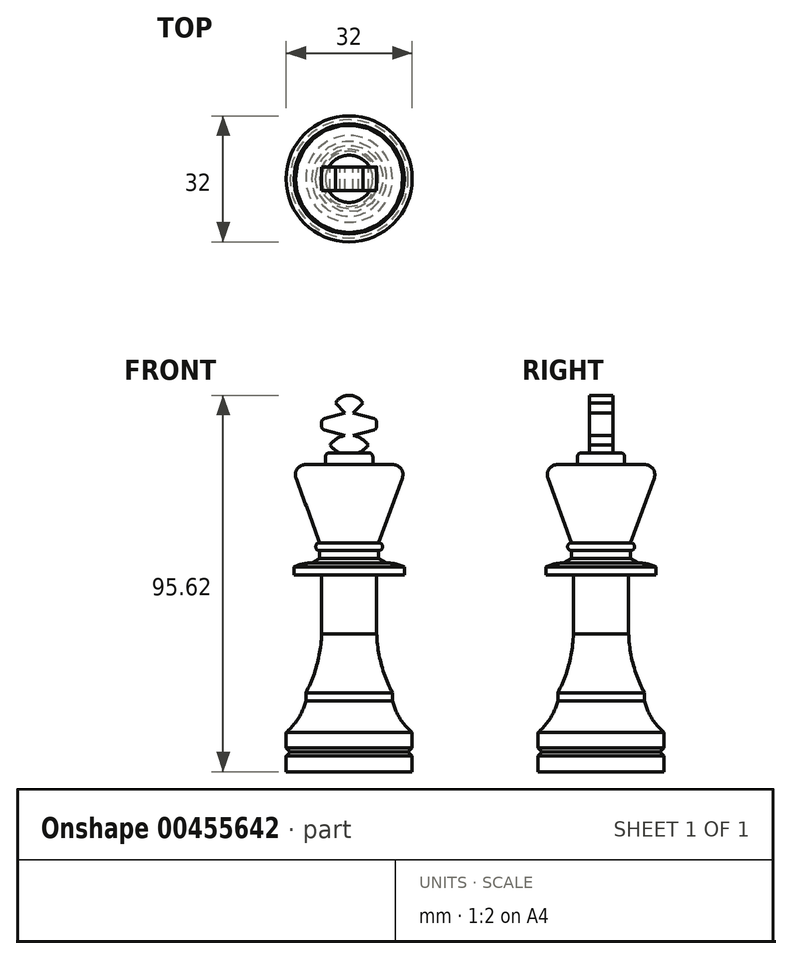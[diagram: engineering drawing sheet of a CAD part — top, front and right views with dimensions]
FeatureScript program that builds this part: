
annotation { "Feature Type Name" : "Feature", "Feature Type Description" : "" }
export const myFeature = defineFeature(function(context is Context, id is Id, definition is map)
    precondition{}
    {
        {
            var Q0;
            Q0=qCreatedBy(makeId("Front.planeOp"),FACE);
            var sketch = newSketch(context, id + "F0", { "sketchPlane" : qUnion([Q0])});
            skLineSegment(sketch, "E0", {"start": v(0, 0) * mm, "end": v(0, 4) * mm});
            skLineSegment(sketch, "E1", {"start": v(0, 4) * mm, "end": v(1, 5) * mm});
            skLineSegment(sketch, "E2", {"start": v(1, 5) * mm, "end": v(0, 6) * mm});
            skLineSegment(sketch, "E3", {"start": v(0, 6) * mm, "end": v(0, 10) * mm});
            skArc(sketch, "E4", {"start": v(0, 10) * mm, "mid": v(3.15, 13.6) * mm, "end": v(5, 18) * mm});
            skLineSegment(sketch, "E5", {"start": v(5, 18) * mm, "end": v(5, 20) * mm});
            skLineSegment(sketch, "E6", {"start": v(5, 20) * mm, "end": v(5, 20) * mm});
            skArc(sketch, "E7", {"start": v(5, 20) * mm, "mid": v(7.84, 27.28) * mm, "end": v(9, 35) * mm});
            skLineSegment(sketch, "E8", {"start": v(16, 0) * mm, "end": v(0, 0) * mm});
            skLineSegment(sketch, "E9", {"start": v(9, 35) * mm, "end": v(9, 50) * mm});
            skLineSegment(sketch, "E10", {"start": v(8.5, 58.16) * mm, "end": v(2.5, 74.64) * mm});
            skLineSegment(sketch, "E11", {"start": v(8.5, 54.16) * mm, "end": v(8.5, 56.16) * mm});
            skArc(sketch, "E12", {"start": v(8.5, 58.16) * mm, "mid": v(7.5, 57.16) * mm, "end": v(8.5, 56.16) * mm});
            skLineSegment(sketch, "E13", {"start": v(4.85, 78) * mm, "end": v(16, 78) * mm});
            skLineSegment(sketch, "E14", {"start": v(16, 0) * mm, "end": v(16, 78) * mm});
            skLineSegment(sketch, "E15", {"start": v(9, 50) * mm, "end": v(2, 50) * mm});
            skLineSegment(sketch, "E16", {"start": v(2, 50) * mm, "end": v(2, 52) * mm});
            skArc(sketch, "E17", {"start": v(4.85, 78) * mm, "mid": v(2.8, 76.93) * mm, "end": v(2.5, 74.64) * mm});
            skArc(sketch, "E18", {"start": v(6.5, 53) * mm, "mid": v(4.2, 52.76) * mm, "end": v(2, 52) * mm});
            skLineSegment(sketch, "E19", {"start": v(6.5, 53) * mm, "end": v(8.5, 54.16) * mm});
            skSolve(sketch);
        }
        {
            var Q0;
            Q0 = qSketchRegion(id + "F0", true);
            var Q1;
            Q1=sQuery(id+"F0.wireOp",EDGE,"E14");
            revolve(context, id + "F1", {"entities" : qUnion([Q0]), "axis" : qUnion([Q1]), "revolveType" : RevolveType.FULL});
        }
        {
            var Q0;
            Q0=makeQuery(id+"F1.opRevolve","SWEPT_FACE",FACE,{"disambiguationData":[OSD([sQuery(id+"F0.wireOp",EDGE,"E13")])]});
            var sketch = newSketch(context, id + "F2", { "sketchPlane" : qUnion([Q0])});
            skCircle(sketch, "E20", {"center": v(16, 0) * mm, "radius": 6 * mm});
            skSolve(sketch);
        }
        {
            var Q0;
            Q0 = qSketchRegion(id + "F2", true);
            extrude(context, id + "F3", {"entities" : qUnion([Q0]), "operationType" : NewBodyOperationType.ADD, "depth" : 3 * mm});
        }
        {
            var Q0;
            Q0=makeQuery(id+"F3.opExtrude","CAP_EDGE",EDGE,{"disambiguationData":[OSD([sQuery(id+"F2.wireOp",EDGE,"E20")])],"isStart":false});
            fillet(context, id + "F4", {"entities" : qUnion([Q0]), "radius" : 1 * mm, "tangentPropagation" : true, "allowEdgeOverflow" : false});
        }
        {
            var Q0;
            Q0=qCreatedBy(makeId("Front.planeOp"),FACE);
            var sketch = newSketch(context, id + "F5", { "sketchPlane" : qUnion([Q0])});
            skArc(sketch, "E21", {"start": v(18.36, 81) * mm, "mid": v(19.75, 81.83) * mm, "end": v(20.86, 83) * mm});
            skArc(sketch, "E22", {"start": v(20.86, 83) * mm, "mid": v(19.17, 84.58) * mm, "end": v(17, 85.4) * mm});
            skLineSegment(sketch, "E23", {"start": v(17, 85.4) * mm, "end": v(23, 87) * mm});
            skLineSegment(sketch, "E24", {"start": v(23, 87) * mm, "end": v(23, 89.5) * mm});
            skLineSegment(sketch, "E25", {"start": v(23, 89.5) * mm, "end": v(17, 91.12) * mm});
            skLineSegment(sketch, "E26", {"start": v(17, 91.12) * mm, "end": v(19.5, 93.62) * mm});
            skArc(sketch, "E27", {"start": v(19.5, 93.62) * mm, "mid": v(18.02, 95.08) * mm, "end": v(16, 95.62) * mm});
            skLineSegment(sketch, "E28", {"start": v(18.36, 81) * mm, "end": v(16, 81) * mm});
            skLineSegment(sketch, "E29", {"start": v(16, 81) * mm, "end": v(16, 95.62) * mm});
            skArc(sketch, "E30.MirrorCS", {"start": v(12.5, 93.62) * mm, "mid": v(13.98, 95.08) * mm, "end": v(16, 95.62) * mm});
            skLineSegment(sketch, "E31.MirrorCS", {"start": v(15, 91.12) * mm, "end": v(12.5, 93.62) * mm});
            skLineSegment(sketch, "E32.MirrorCS", {"start": v(9, 89.5) * mm, "end": v(15, 91.12) * mm});
            skLineSegment(sketch, "E33.MirrorCS", {"start": v(9, 87) * mm, "end": v(9, 89.5) * mm});
            skLineSegment(sketch, "E34.MirrorCS", {"start": v(15, 85.4) * mm, "end": v(9, 87) * mm});
            skArc(sketch, "E35.MirrorCS", {"start": v(11.14, 83) * mm, "mid": v(12.83, 84.58) * mm, "end": v(15, 85.4) * mm});
            skArc(sketch, "E36.MirrorCS", {"start": v(13.64, 81) * mm, "mid": v(12.25, 81.83) * mm, "end": v(11.14, 83) * mm});
            skLineSegment(sketch, "E37.MirrorCS", {"start": v(13.64, 81) * mm, "end": v(16, 81) * mm});
            skSolve(sketch);
        }
        {
            var Q0;
            Q0 = qSketchRegion(id + "F5", true);
            extrude(context, id + "F6", {"entities" : qUnion([Q0]), "depth" : 3 * mm, "hasSecondDirection" : true, "secondDirectionOppositeDirection" : true, "secondDirectionDepth" : 3 * mm});
        }
        {
            var Q0;
            Q0=makeQuery(id+"F6.opExtrude","SWEPT_EDGE",EDGE,{"disambiguationData":[OSD([sQuery(id+"F5.wireOp",EDGE,"E24"),sQuery(id+"F5.wireOp",EDGE,"E25")])]});
            var Q1;
            Q1=makeQuery(id+"F6.opExtrude","SWEPT_EDGE",EDGE,{"disambiguationData":[OSD([sQuery(id+"F5.wireOp",EDGE,"E23"),sQuery(id+"F5.wireOp",EDGE,"E24")])]});
            var Q2;
            Q2=makeQuery(id+"F6.opExtrude","SWEPT_EDGE",EDGE,{"disambiguationData":[OSD([sQuery(id+"F5.wireOp",EDGE,"E32.MirrorCS"),sQuery(id+"F5.wireOp",EDGE,"E33.MirrorCS")])]});
            var Q3;
            Q3=makeQuery(id+"F6.opExtrude","SWEPT_EDGE",EDGE,{"disambiguationData":[OSD([sQuery(id+"F5.wireOp",EDGE,"E33.MirrorCS"),sQuery(id+"F5.wireOp",EDGE,"E34.MirrorCS")])]});
            fillet(context, id + "F7", {"entities" : qUnion([Q0, Q1, Q2, Q3]), "radius" : 1 * mm, "tangentPropagation" : true, "allowEdgeOverflow" : false});
        }
    });
